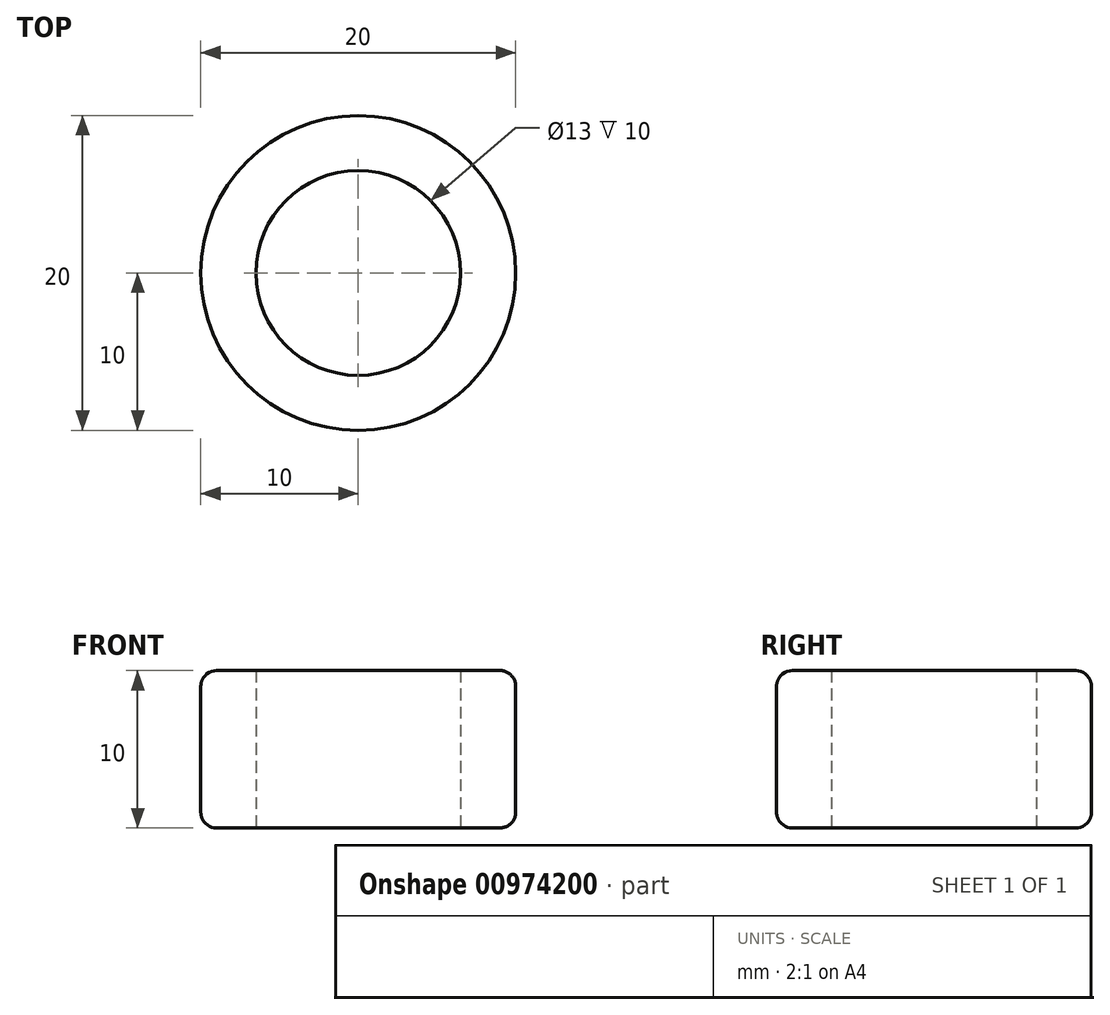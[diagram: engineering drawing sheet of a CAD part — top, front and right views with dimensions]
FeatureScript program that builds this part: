
annotation { "Feature Type Name" : "Feature", "Feature Type Description" : "" }
export const myFeature = defineFeature(function(context is Context, id is Id, definition is map)
    precondition{}
    {
        {
            var Q0;
            Q0=qCreatedBy(makeId("Top.planeOp"),FACE);
            var sketch = newSketch(context, id + "F0", { "sketchPlane" : qUnion([Q0])});
            skCircle(sketch, "E0", {"center": v(0, 0) * mm, "radius": 10 * mm});
            skCircle(sketch, "E1", {"center": v(0, 0) * mm, "radius": 6.5 * mm});
            skSolve(sketch);
        }
        {
            var Q0;
            Q0=makeQuery(id+"F0.imprint","IMPRINT",FACE,{"disambiguationData":[TD([[makeQuery(id+"F0.imprint","IMPRINT",EDGE,{"derivedFrom":sQuery(id+"F0.wireOp",EDGE,"E0")}),1.0]])]});
            var Q1;
            Q1=sQuery(id+"F0.wireOp",EDGE,"E1");
            var Q2;
            Q2=sQuery(id+"F0.wireOp",EDGE,"E0");
            extrude(context, id + "F1", {"entities" : qUnion([Q0]), "surfaceEntities" : qUnion([Q1, Q2]), "depth" : 10 * mm, "offsetDistance" : 25 * mm});
        }
        {
            var Q0;
            Q0=makeQuery(id+"F1.opExtrude","CAP_EDGE",EDGE,{"disambiguationData":[OSD([sQuery(id+"F0.wireOp",EDGE,"E0")])],"isStart":false});
            fillet(context, id + "F2", {"entities" : qUnion([Q0]), "radius" : 1 * mm, "tangentPropagation" : true, "allowEdgeOverflow" : false});
        }
        {
            var Q0;
            Q0=makeQuery(id+"F1.opExtrude","CAP_EDGE",EDGE,{"disambiguationData":[OSD([sQuery(id+"F0.wireOp",EDGE,"E0")])],"isStart":true});
            fillet(context, id + "F3", {"entities" : qUnion([Q0]), "radius" : 1 * mm, "tangentPropagation" : true, "allowEdgeOverflow" : false});
        }
    });
